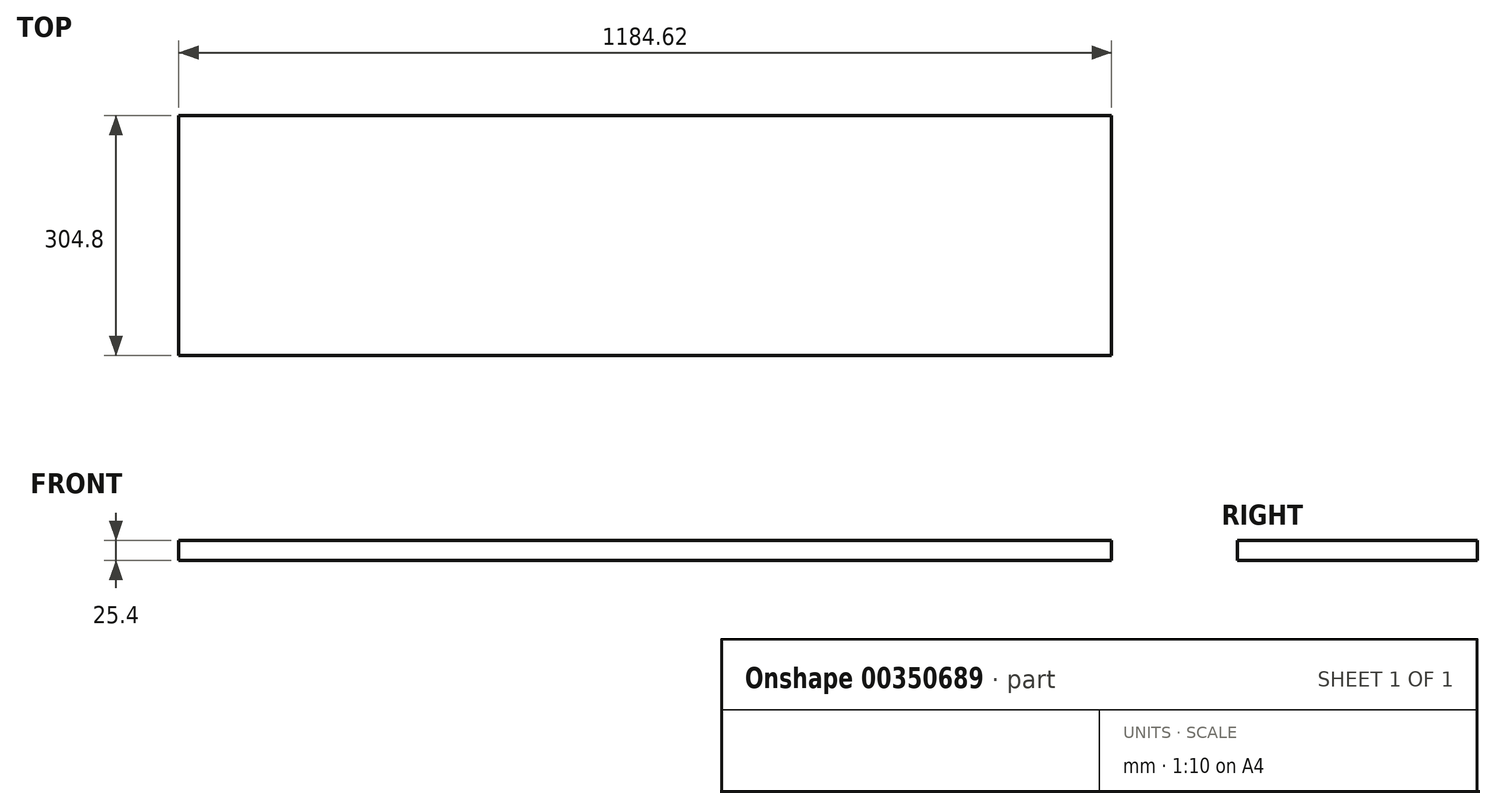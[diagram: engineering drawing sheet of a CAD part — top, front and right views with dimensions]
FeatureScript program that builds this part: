
annotation { "Feature Type Name" : "Feature", "Feature Type Description" : "" }
export const myFeature = defineFeature(function(context is Context, id is Id, definition is map)
    precondition{}
    {
        {
            var Q0;
            Q0=qCreatedBy(makeId("Front.planeOp"),FACE);
            var sketch = newSketch(context, id + "F0", { "sketchPlane" : qUnion([Q0])});
            skLineSegment(sketch, "E0", {"start": v(-457.2, 0) * mm, "end": v(457.2, 0) * mm});
            skLineSegment(sketch, "E1.bottom", {"start": v(-457.2, 0) * mm, "end": v(727.42, 0) * mm});
            skLineSegment(sketch, "E1.top", {"start": v(-457.2, -25.4) * mm, "end": v(727.42, -25.4) * mm});
            skLineSegment(sketch, "E1.left", {"start": v(-457.2, 0) * mm, "end": v(-457.2, -25.4) * mm});
            skLineSegment(sketch, "E1.right", {"start": v(727.42, 0) * mm, "end": v(727.42, -25.4) * mm});
            skSolve(sketch);
        }
        {
            var Q0;
            Q0=makeQuery(id+"F0.imprint","IMPRINT",FACE,{"disambiguationData":[TD([[makeQuery(id+"F0.imprint","IMPRINT",EDGE,{"derivedFrom":sQuery(id+"F0.wireOp",EDGE,"E1.top")}),1.0]])]});
            extrude(context, id + "F1", {"entities" : qUnion([Q0]), "oppositeDirection" : true, "depth" : 304.8 * mm});
        }
    });
